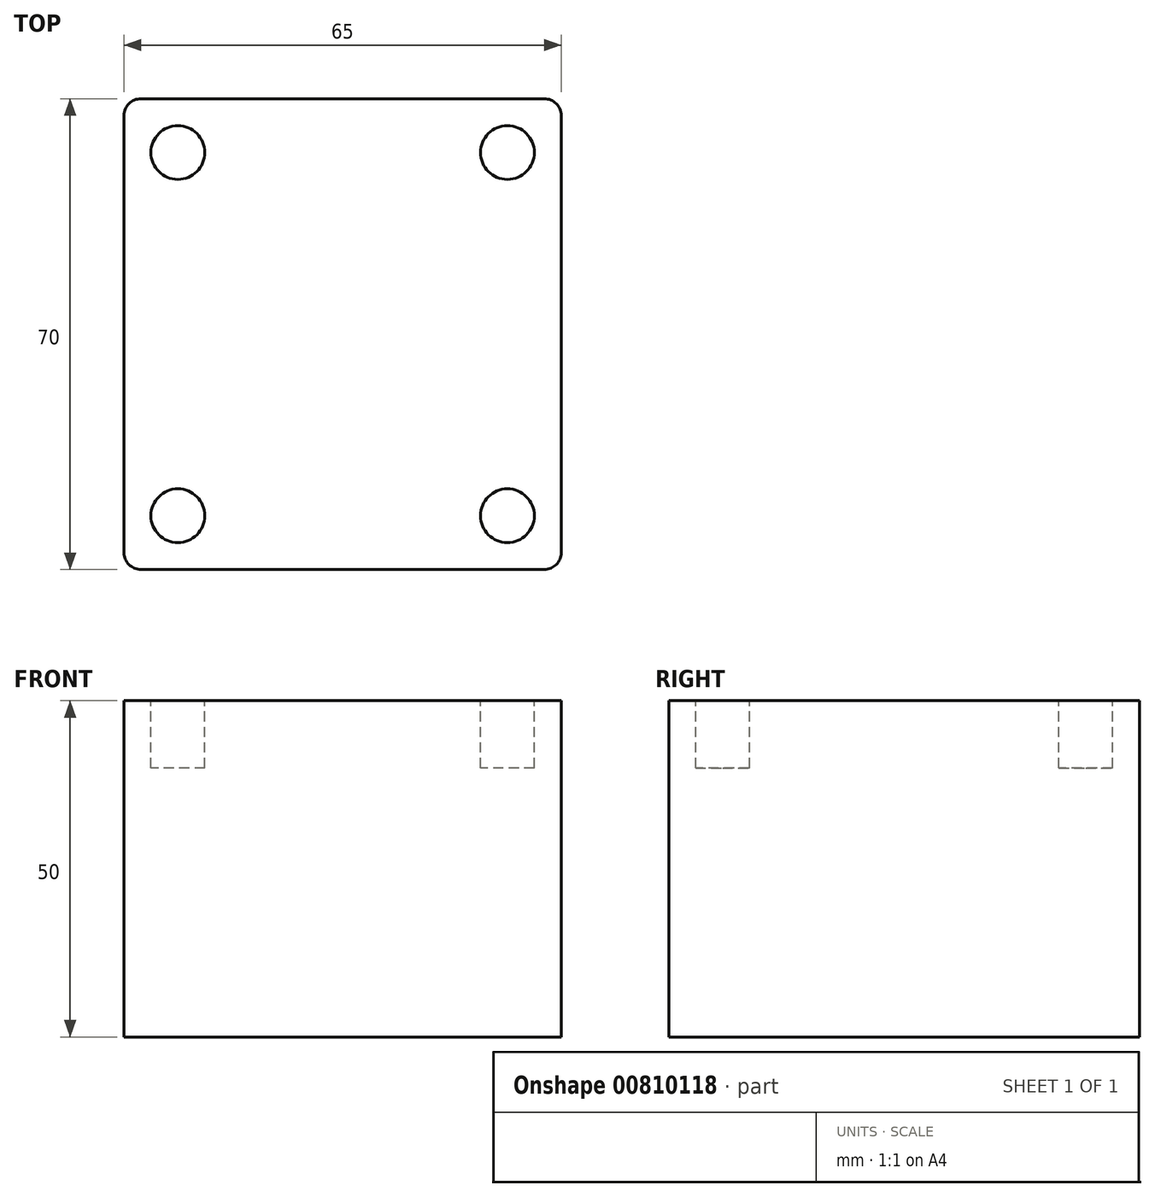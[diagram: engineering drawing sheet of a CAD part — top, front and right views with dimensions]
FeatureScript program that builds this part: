
annotation { "Feature Type Name" : "Feature", "Feature Type Description" : "" }
export const myFeature = defineFeature(function(context is Context, id is Id, definition is map)
    precondition{}
    {
        {
            var Q0;
            Q0=qCreatedBy(makeId("Top.planeOp"),FACE);
            var sketch = newSketch(context, id + "F0", { "sketchPlane" : qUnion([Q0])});
            skLineSegment(sketch, "E0.bottom", {"start": v(-30, 35) * mm, "end": v(30, 35) * mm});
            skLineSegment(sketch, "E0.top", {"start": v(-30, -35) * mm, "end": v(30, -35) * mm});
            skLineSegment(sketch, "E0.left", {"start": v(-32.5, 32.5) * mm, "end": v(-32.5, -32.5) * mm});
            skLineSegment(sketch, "E0.right", {"start": v(32.5, 32.5) * mm, "end": v(32.5, -32.5) * mm});
            skPoint(sketch, "E0.middle", {"position": v(0, 0) * mm});
            skPoint(sketch, "E1", {"position": v(-24.5, 27) * mm});
            skPoint(sketch, "E2.MirrorP", {"position": v(24.5, 27) * mm});
            skPoint(sketch, "E3.MirrorP", {"position": v(24.5, -27) * mm});
            skPoint(sketch, "E4.MirrorP", {"position": v(-24.5, -27) * mm});
            skPoint(sketch, "E5.visualSharp", {"position": v(-32.5, 35) * mm});
            skArc(sketch, "E5.filletArc", {"start": v(-30, 35) * mm, "mid": v(-31.77, 34.27) * mm, "end": v(-32.5, 32.5) * mm});
            skPoint(sketch, "E6.visualSharp", {"position": v(32.5, 35) * mm});
            skArc(sketch, "E6.filletArc", {"start": v(32.5, 32.5) * mm, "mid": v(31.77, 34.27) * mm, "end": v(30, 35) * mm});
            skPoint(sketch, "E7.visualSharp", {"position": v(32.5, -35) * mm});
            skArc(sketch, "E7.filletArc", {"start": v(30, -35) * mm, "mid": v(31.77, -34.27) * mm, "end": v(32.5, -32.5) * mm});
            skPoint(sketch, "E8.visualSharp", {"position": v(-32.5, -35) * mm});
            skArc(sketch, "E8.filletArc", {"start": v(-32.5, -32.5) * mm, "mid": v(-31.77, -34.27) * mm, "end": v(-30, -35) * mm});
            skSolve(sketch);
        }
        {
            var Q0;
            Q0=makeQuery(id+"F0.imprint","IMPRINT",FACE,{"disambiguationData":[TD([[makeQuery(id+"F0.imprint","IMPRINT",EDGE,{"derivedFrom":sQuery(id+"F0.wireOp",EDGE,"E0.bottom")}),-1.0]])]});
            extrude(context, id + "F1", {"entities" : qUnion([Q0]), "depth" : 10 * mm, "offsetDistance" : 25 * mm});
        }
        {
            var Q0;
            Q0=sQuery(id+"F0.wireOp",VERTEX,"E2.MirrorP");
            var Q1;
            Q1=makeQuery(id+"F1.opExtrude","SWEPT_BODY",BODY,{"disambiguationData":[OSD([sQuery(id+"F0.wireOp",EDGE,"E0.bottom"),sQuery(id+"F0.wireOp",EDGE,"E0.top"),sQuery(id+"F0.wireOp",EDGE,"E0.left"),sQuery(id+"F0.wireOp",EDGE,"E0.right"),sQuery(id+"F0.wireOp",EDGE,"E5.filletArc"),sQuery(id+"F0.wireOp",EDGE,"E6.filletArc"),sQuery(id+"F0.wireOp",EDGE,"E7.filletArc"),sQuery(id+"F0.wireOp",EDGE,"E8.filletArc")])]});
            hole(context, id + "F2", {"style" : HoleStyle.SIMPLE, "endStyle" : HoleEndStyle.THROUGH, "oppositeDirection" : true, "holeDiameter" : 8 * mm, "majorDiameter" : 5 * mm, "isTappedThrough" : true, "tappedDepth" : 12 * mm, "tapClearance" : 3, "locations" : qUnion([Q0]), "scope" : qUnion([Q1])});
        }
        {
            var Q0;
            Q0=sQuery(id+"F0.wireOp",VERTEX,"E1");
            var Q1;
            Q1=makeQuery(id+"F1.opExtrude","SWEPT_BODY",BODY,{"disambiguationData":[OSD([sQuery(id+"F0.wireOp",EDGE,"E0.bottom"),sQuery(id+"F0.wireOp",EDGE,"E0.top"),sQuery(id+"F0.wireOp",EDGE,"E0.left"),sQuery(id+"F0.wireOp",EDGE,"E0.right"),sQuery(id+"F0.wireOp",EDGE,"E5.filletArc"),sQuery(id+"F0.wireOp",EDGE,"E6.filletArc"),sQuery(id+"F0.wireOp",EDGE,"E7.filletArc"),sQuery(id+"F0.wireOp",EDGE,"E8.filletArc")])]});
            hole(context, id + "F3", {"style" : HoleStyle.SIMPLE, "endStyle" : HoleEndStyle.THROUGH, "oppositeDirection" : true, "holeDiameter" : 8 * mm, "majorDiameter" : 5 * mm, "isTappedThrough" : true, "tappedDepth" : 12 * mm, "tapClearance" : 3, "locations" : qUnion([Q0]), "scope" : qUnion([Q1])});
        }
        {
            var Q0;
            Q0=sQuery(id+"F0.wireOp",VERTEX,"E3.MirrorP");
            var Q1;
            Q1=makeQuery(id+"F1.opExtrude","SWEPT_BODY",BODY,{"disambiguationData":[OSD([sQuery(id+"F0.wireOp",EDGE,"E0.bottom"),sQuery(id+"F0.wireOp",EDGE,"E0.top"),sQuery(id+"F0.wireOp",EDGE,"E0.left"),sQuery(id+"F0.wireOp",EDGE,"E0.right"),sQuery(id+"F0.wireOp",EDGE,"E5.filletArc"),sQuery(id+"F0.wireOp",EDGE,"E6.filletArc"),sQuery(id+"F0.wireOp",EDGE,"E7.filletArc"),sQuery(id+"F0.wireOp",EDGE,"E8.filletArc")])]});
            hole(context, id + "F4", {"style" : HoleStyle.SIMPLE, "endStyle" : HoleEndStyle.THROUGH, "oppositeDirection" : true, "holeDiameter" : 8 * mm, "majorDiameter" : 5 * mm, "isTappedThrough" : true, "tappedDepth" : 12 * mm, "tapClearance" : 3, "locations" : qUnion([Q0]), "scope" : qUnion([Q1])});
        }
        {
            var Q0;
            Q0=sQuery(id+"F0.wireOp",VERTEX,"E4.MirrorP");
            var Q1;
            Q1=makeQuery(id+"F1.opExtrude","SWEPT_BODY",BODY,{"disambiguationData":[OSD([sQuery(id+"F0.wireOp",EDGE,"E0.bottom"),sQuery(id+"F0.wireOp",EDGE,"E0.top"),sQuery(id+"F0.wireOp",EDGE,"E0.left"),sQuery(id+"F0.wireOp",EDGE,"E0.right"),sQuery(id+"F0.wireOp",EDGE,"E5.filletArc"),sQuery(id+"F0.wireOp",EDGE,"E6.filletArc"),sQuery(id+"F0.wireOp",EDGE,"E7.filletArc"),sQuery(id+"F0.wireOp",EDGE,"E8.filletArc")])]});
            hole(context, id + "F5", {"style" : HoleStyle.SIMPLE, "endStyle" : HoleEndStyle.THROUGH, "oppositeDirection" : true, "holeDiameter" : 8 * mm, "majorDiameter" : 5 * mm, "isTappedThrough" : true, "tappedDepth" : 12 * mm, "tapClearance" : 3, "locations" : qUnion([Q0]), "scope" : qUnion([Q1])});
        }
        {
            var Q0;
            Q0=qCreatedBy(makeId("Top.planeOp"),FACE);
            var sketch = newSketch(context, id + "F6", { "sketchPlane" : qUnion([Q0])});
            skLineSegment(sketch, "E9.bottom", {"start": v(-15, 33) * mm, "end": v(15, 33) * mm});
            skLineSegment(sketch, "E9.top", {"start": v(-15, -33) * mm, "end": v(15, -33) * mm});
            skLineSegment(sketch, "E9.left", {"start": v(-15, 33) * mm, "end": v(-15, -33) * mm});
            skLineSegment(sketch, "E9.right", {"start": v(15, 33) * mm, "end": v(15, -33) * mm});
            skPoint(sketch, "E9.middle", {"position": v(0, 0) * mm});
            skLineSegment(sketch, "E10.bottom", {"start": v(15, 33) * mm, "end": v(15, 33) * mm});
            skLineSegment(sketch, "E10.top", {"start": v(15, -40.22) * mm, "end": v(15, -40.22) * mm});
            skLineSegment(sketch, "E11.left", {"start": v(15, 40.48) * mm, "end": v(15, 40.06) * mm});
            skLineSegment(sketch, "E11.right", {"start": v(32.57, 40.48) * mm, "end": v(32.57, 40.06) * mm});
            skLineSegment(sketch, "E12.right", {"start": v(33.59, -40.22) * mm, "end": v(33.59, -40.22) * mm});
            skLineSegment(sketch, "E13.bottom", {"start": v(15, 40.06) * mm, "end": v(15, 40.06) * mm});
            skSolve(sketch);
        }
        {
            var Q0;
            Q0=makeQuery(id+"F6.imprint","IMPRINT",FACE,{"disambiguationData":[TD([[makeQuery(id+"F6.imprint","IMPRINT",EDGE,{"derivedFrom":sQuery(id+"F6.wireOp",EDGE,"E9.bottom")}),-1.0]])]});
            var Q1;
            Q1 = qSketchRegion(id + "F0", true);
            extrude(context, id + "F7", {"entities" : qUnion([Q0, Q1]), "operationType" : NewBodyOperationType.ADD, "oppositeDirection" : true, "depth" : 40 * mm, "offsetDistance" : 25 * mm});
        }
    });
